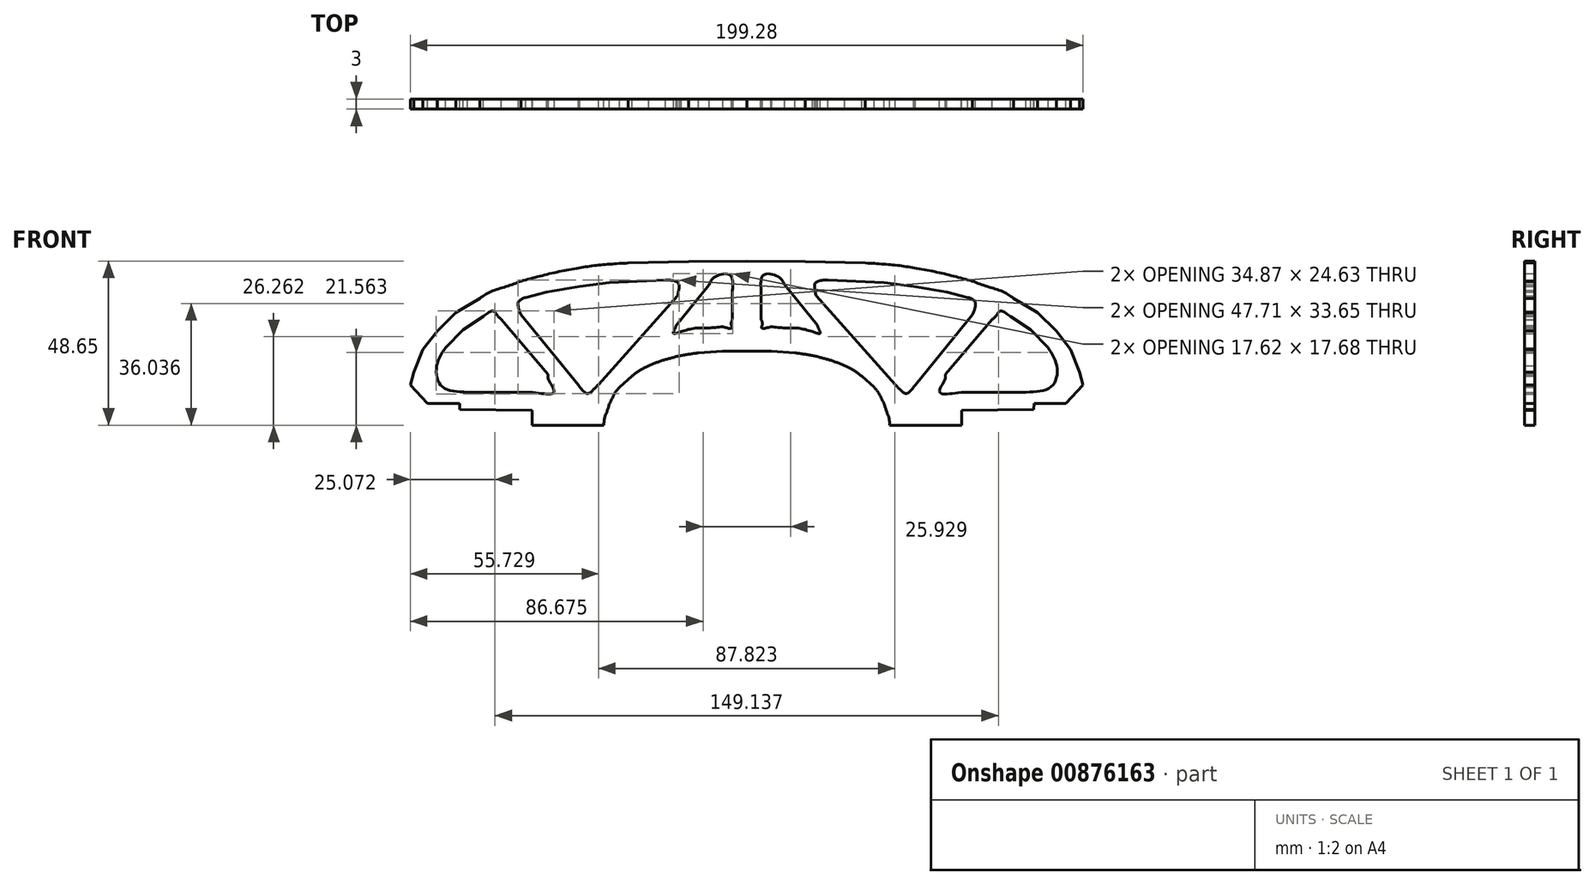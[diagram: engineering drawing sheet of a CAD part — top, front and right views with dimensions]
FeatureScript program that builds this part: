
annotation { "Feature Type Name" : "Feature", "Feature Type Description" : "" }
export const myFeature = defineFeature(function(context is Context, id is Id, definition is map)
    precondition{}
    {
        {
            var Q0;
            Q0=qCreatedBy(makeId("Front.planeOp"),FACE);
            var sketch = newSketch(context, id + "F0", { "sketchPlane" : qUnion([Q0])});
            skLineSegment(sketch, "E0", {"start": v(0, 22.63) * mm, "end": v(17.3, 22.49) * mm});
            skLineSegment(sketch, "E1", {"start": v(17.3, 22.49) * mm, "end": v(35.15, 22.06) * mm});
            skLineSegment(sketch, "E2", {"start": v(79.1, 11.57) * mm, "end": v(86.18, 7.32) * mm});
            skLineSegment(sketch, "E3", {"start": v(86.18, 7.32) * mm, "end": v(91.7, 1.94) * mm});
            skLineSegment(sketch, "E4", {"start": v(91.7, 1.94) * mm, "end": v(95.96, -3.6) * mm});
            skLineSegment(sketch, "E5", {"start": v(95.96, -3.6) * mm, "end": v(98.65, -10.25) * mm});
            skLineSegment(sketch, "E6", {"start": v(98.65, -10.25) * mm, "end": v(99.64, -14.08) * mm});
            skLineSegment(sketch, "E7", {"start": v(99.64, -14.08) * mm, "end": v(94.52, -19.52) * mm});
            skLineSegment(sketch, "E8", {"start": v(94.52, -19.52) * mm, "end": v(85.08, -19.62) * mm});
            skLineSegment(sketch, "E9", {"start": v(85.08, -19.62) * mm, "end": v(85.06, -21.4) * mm});
            skLineSegment(sketch, "E10", {"start": v(85.06, -21.4) * mm, "end": v(63.64, -21.6) * mm});
            skLineSegment(sketch, "E11", {"start": v(63.64, -21.6) * mm, "end": v(63.64, -25.99) * mm});
            skLineSegment(sketch, "E12", {"start": v(63.64, -25.99) * mm, "end": v(42.35, -26.02) * mm});
            skLineSegment(sketch, "E13", {"start": v(37.7, -14.75) * mm, "end": v(34.02, -11.39) * mm});
            skLineSegment(sketch, "E14", {"start": v(14.32, -4.58) * mm, "end": v(7.23, -4.07) * mm});
            skLineSegment(sketch, "E15", {"start": v(7.23, -4.07) * mm, "end": v(0, -4.02) * mm});
            skLineSegment(sketch, "E16", {"start": v(11.16, 15.58) * mm, "end": v(20.94, 3.53) * mm});
            skLineSegment(sketch, "E17", {"start": v(4.25, 5.2) * mm, "end": v(4.25, 13.91) * mm});
            skLineSegment(sketch, "E18", {"start": v(24.1, 17.07) * mm, "end": v(40.68, 16.25) * mm});
            skLineSegment(sketch, "E19", {"start": v(40.68, 16.25) * mm, "end": v(49.47, 15.12) * mm});
            skLineSegment(sketch, "E20", {"start": v(49.47, 15.12) * mm, "end": v(59.25, 13.42) * mm});
            skLineSegment(sketch, "E21", {"start": v(59.25, 13.42) * mm, "end": v(65.48, 11.86) * mm});
            skLineSegment(sketch, "E22", {"start": v(66.9, 6.76) * mm, "end": v(49.9, -14.08) * mm});
            skLineSegment(sketch, "E23", {"start": v(43.94, -13.94) * mm, "end": v(20.55, 12.28) * mm});
            skLineSegment(sketch, "E24", {"start": v(78.1, 6.19) * mm, "end": v(84.05, 2.22) * mm});
            skLineSegment(sketch, "E25", {"start": v(84.05, 2.22) * mm, "end": v(89.3, -3.02) * mm});
            skLineSegment(sketch, "E26", {"start": v(82.78, -16.2) * mm, "end": v(63.5, -16.2) * mm});
            skLineSegment(sketch, "E27", {"start": v(58.82, -10.96) * mm, "end": v(72.71, 5.34) * mm});
            skFitSpline(sketch, "E28", {"points": [v(35.15, 22.06) * mm, v(40.41, 21.73) * mm, v(45.53, 21.24) * mm, v(50.4, 20.45) * mm]});
            skFitSpline(sketch, "E29", {"points": [v(50.4, 20.45) * mm, v(56.17, 19.38) * mm, v(61.6, 18.07) * mm, v(66.9, 16.68) * mm]});
            skFitSpline(sketch, "E30", {"points": [v(66.9, 16.68) * mm, v(71.16, 15.11) * mm, v(75.69, 13.61) * mm, v(79.1, 11.57) * mm]});
            skFitSpline(sketch, "E31", {"points": [v(42.35, -26.02) * mm, v(42.13, -23.9) * mm, v(41.38, -21.83) * mm, v(40.72, -19.75) * mm]});
            skFitSpline(sketch, "E32", {"points": [v(40.72, -19.75) * mm, v(39.9, -18.12) * mm, v(39.07, -16.48) * mm, v(37.7, -14.75) * mm]});
            skFitSpline(sketch, "E33", {"points": [v(34.02, -11.39) * mm, v(32.66, -10.45) * mm, v(31.26, -9.51) * mm, v(29.06, -8.41) * mm]});
            skFitSpline(sketch, "E34", {"points": [v(29.06, -8.41) * mm, v(26.84, -7.47) * mm, v(24.53, -6.67) * mm, v(22.11, -6) * mm]});
            skFitSpline(sketch, "E35", {"points": [v(22.11, -6) * mm, v(19.59, -5.38) * mm, v(16.97, -4.94) * mm, v(14.32, -4.58) * mm]});
            skFitSpline(sketch, "E36", {"points": [v(4.25, 13.91) * mm, v(5.03, 18.52) * mm, v(9.46, 17.95) * mm, v(11.16, 15.58) * mm]});
            skFitSpline(sketch, "E37", {"points": [v(20.94, 3.53) * mm, v(21.35, 2.49) * mm, v(21.75, 1.24) * mm, v(19.43, 1.75) * mm]});
            skFitSpline(sketch, "E38", {"points": [v(19.43, 1.75) * mm, v(15.42, 2.71) * mm, v(11.24, 2.83) * mm, v(7.1, 3.17) * mm]});
            skFitSpline(sketch, "E39", {"points": [v(7.1, 3.17) * mm, v(4.45, 2.8) * mm, v(4.64, 4.04) * mm, v(4.25, 5.2) * mm]});
            skFitSpline(sketch, "E40", {"points": [v(65.48, 11.86) * mm, v(67.53, 10.68) * mm, v(67.65, 8.86) * mm, v(66.9, 6.76) * mm]});
            skFitSpline(sketch, "E41", {"points": [v(49.9, -14.08) * mm, v(47.3, -16.6) * mm, v(45.55, -15.58) * mm, v(43.94, -13.94) * mm]});
            skFitSpline(sketch, "E42", {"points": [v(20.55, 12.28) * mm, v(20.07, 14.68) * mm, v(20.54, 16.36) * mm, v(24.1, 17.07) * mm]});
            skFitSpline(sketch, "E43", {"points": [v(89.3, -3.02) * mm, v(91.92, -8.82) * mm, v(90.28, -14.53) * mm, v(82.78, -16.2) * mm]});
            skFitSpline(sketch, "E44", {"points": [v(63.5, -16.2) * mm, v(57.14, -16.16) * mm, v(58.7, -12.47) * mm, v(58.82, -10.96) * mm]});
            skFitSpline(sketch, "E45", {"points": [v(72.71, 5.34) * mm, v(73.96, 6.55) * mm, v(75.16, 7.84) * mm, v(78.1, 6.19) * mm]});
            skLineSegment(sketch, "E46", {"start": v(0, 22.63) * mm, "end": v(0, -4.02) * mm});
            skSolve(sketch);
        }
        {
            var Q0;
            Q0 = qSketchRegion(id + "F0", true);
            extrude(context, id + "F1", {"entities" : qUnion([Q0]), "depth" : 3 * mm, "offsetDistance" : 25 * mm});
        }
        {
            var Q0;
            Q0=makeQuery(id+"F1.opExtrude","SWEPT_BODY",BODY,{"disambiguationData":[OSD([sQuery(id+"F0.wireOp",EDGE,"E0"),sQuery(id+"F0.wireOp",EDGE,"E1"),sQuery(id+"F0.wireOp",EDGE,"E2"),sQuery(id+"F0.wireOp",EDGE,"E3"),sQuery(id+"F0.wireOp",EDGE,"E4"),sQuery(id+"F0.wireOp",EDGE,"E5"),sQuery(id+"F0.wireOp",EDGE,"E6"),sQuery(id+"F0.wireOp",EDGE,"E7"),sQuery(id+"F0.wireOp",EDGE,"E8"),sQuery(id+"F0.wireOp",EDGE,"E9"),sQuery(id+"F0.wireOp",EDGE,"E10"),sQuery(id+"F0.wireOp",EDGE,"E11"),sQuery(id+"F0.wireOp",EDGE,"E12"),sQuery(id+"F0.wireOp",EDGE,"E13"),sQuery(id+"F0.wireOp",EDGE,"E14"),sQuery(id+"F0.wireOp",EDGE,"E15"),sQuery(id+"F0.wireOp",EDGE,"E16"),sQuery(id+"F0.wireOp",EDGE,"E17"),sQuery(id+"F0.wireOp",EDGE,"E18"),sQuery(id+"F0.wireOp",EDGE,"E19"),sQuery(id+"F0.wireOp",EDGE,"E20"),sQuery(id+"F0.wireOp",EDGE,"E21"),sQuery(id+"F0.wireOp",EDGE,"E22"),sQuery(id+"F0.wireOp",EDGE,"E23"),sQuery(id+"F0.wireOp",EDGE,"E24"),sQuery(id+"F0.wireOp",EDGE,"E25"),sQuery(id+"F0.wireOp",EDGE,"E26"),sQuery(id+"F0.wireOp",EDGE,"E27"),sQuery(id+"F0.wireOp",EDGE,"E28"),sQuery(id+"F0.wireOp",EDGE,"E29"),sQuery(id+"F0.wireOp",EDGE,"E30"),sQuery(id+"F0.wireOp",EDGE,"E31"),sQuery(id+"F0.wireOp",EDGE,"E32"),sQuery(id+"F0.wireOp",EDGE,"E33"),sQuery(id+"F0.wireOp",EDGE,"E34"),sQuery(id+"F0.wireOp",EDGE,"E35"),sQuery(id+"F0.wireOp",EDGE,"E36"),sQuery(id+"F0.wireOp",EDGE,"E37"),sQuery(id+"F0.wireOp",EDGE,"E38"),sQuery(id+"F0.wireOp",EDGE,"E39"),sQuery(id+"F0.wireOp",EDGE,"E40"),sQuery(id+"F0.wireOp",EDGE,"E41"),sQuery(id+"F0.wireOp",EDGE,"E42"),sQuery(id+"F0.wireOp",EDGE,"E43"),sQuery(id+"F0.wireOp",EDGE,"E44"),sQuery(id+"F0.wireOp",EDGE,"E45"),sQuery(id+"F0.wireOp",EDGE,"E46")])]});
            var Q1;
            Q1=qCreatedBy(makeId("Right.planeOp"),FACE);
            mirror(context, id + "F2", {"operationType" : NewBodyOperationType.ADD, "entities" : qUnion([Q0]), "mirrorPlane" : qUnion([Q1])});
        }
    });
